FCSTD DOCUMENT  (FreeCAD 1.1R20260108 (Git shallow))
Label: 001_MasterSketch_PistonHead
License: All rights reserved
LicenseURL: http://en.wikipedia.org/wiki/All_rights_reserved
objects: Sketcher::SketchObject×1
note: 2 computed .brp shape members not serialized (recipe doc carries the construction recipe); baked Part::Feature solids carry a one-line shape summary decoded from their .brp

FEATURE [Sketcher::SketchObject] Sketch
  ArcFitTolerance = 1e-06
  ExternalTypes = [0]
  FullyConstrained = true
  MakeInternals = false
  sketch-geometry (10):
    g0: ArcOfCircle CenterX=0 CenterY=55 CenterZ=0 NormalX=0 NormalY=0 NormalZ=1 AngleXU=0 Radius=10 StartAngle=8e-16 EndAngle=3.14159
    g1: ArcOfCircle CenterX=0 CenterY=-55 CenterZ=0 NormalX=0 NormalY=0 NormalZ=1 AngleXU=0 Radius=10 StartAngle=3.14159 EndAngle=6.28319
    g2: LineSegment StartX=10 StartY=55 StartZ=0 EndX=10 EndY=-55 EndZ=0
    g3: LineSegment StartX=-10 StartY=55 StartZ=0 EndX=-10 EndY=-55 EndZ=0
    g4: Circle CenterX=0 CenterY=55 CenterZ=0 NormalX=0 NormalY=0 NormalZ=1 AngleXU=0 Radius=3.5
    g5: Circle CenterX=0 CenterY=-55 CenterZ=0 NormalX=0 NormalY=0 NormalZ=1 AngleXU=0 Radius=3.5
    g6: LineSegment StartX=-30 StartY=80 StartZ=0 EndX=-30 EndY=20 EndZ=0
    g7: LineSegment StartX=-30 StartY=20 StartZ=0 EndX=30 EndY=20 EndZ=0
    g8: LineSegment StartX=30 StartY=20 StartZ=0 EndX=30 EndY=80 EndZ=0
    g9: LineSegment StartX=30 StartY=80 StartZ=0 EndX=-30 EndY=80 EndZ=0
  constraints (24):
    c: Tangent(g0,g2) = 1.5708
    c: Tangent(g0,g3) = -1.5708
    c: Tangent(g1,g2) = 1.5708
    c: Tangent(g1,g3) = -1.5708
    c: Equal(g0,g1)
    c: Vertical(g2)
    c: DistanceY(g1,g0) = 110
    c: Coincident(g4,g0)
    c: Coincident(g5,g1)
    c: Equal(g5,g4)
    c: Diameter(g4) = 7
    c: Radius(g0) = 10
    c: Symmetric(g0,g1,g-1)
    c: Coincident(g6,g7)
    c: Coincident(g7,g8)
    c: Coincident(g8,g9)
    c: Coincident(g9,g6)
    c: Vertical(g6)
    c: Vertical(g8)
    c: Horizontal(g7)
    c: Distance(g6,g8) = 60
    c: Equal(g6,g9)
    c: Symmetric(g6,g8,g-2)
    c: DistanceY(g-1,g6) = 20
